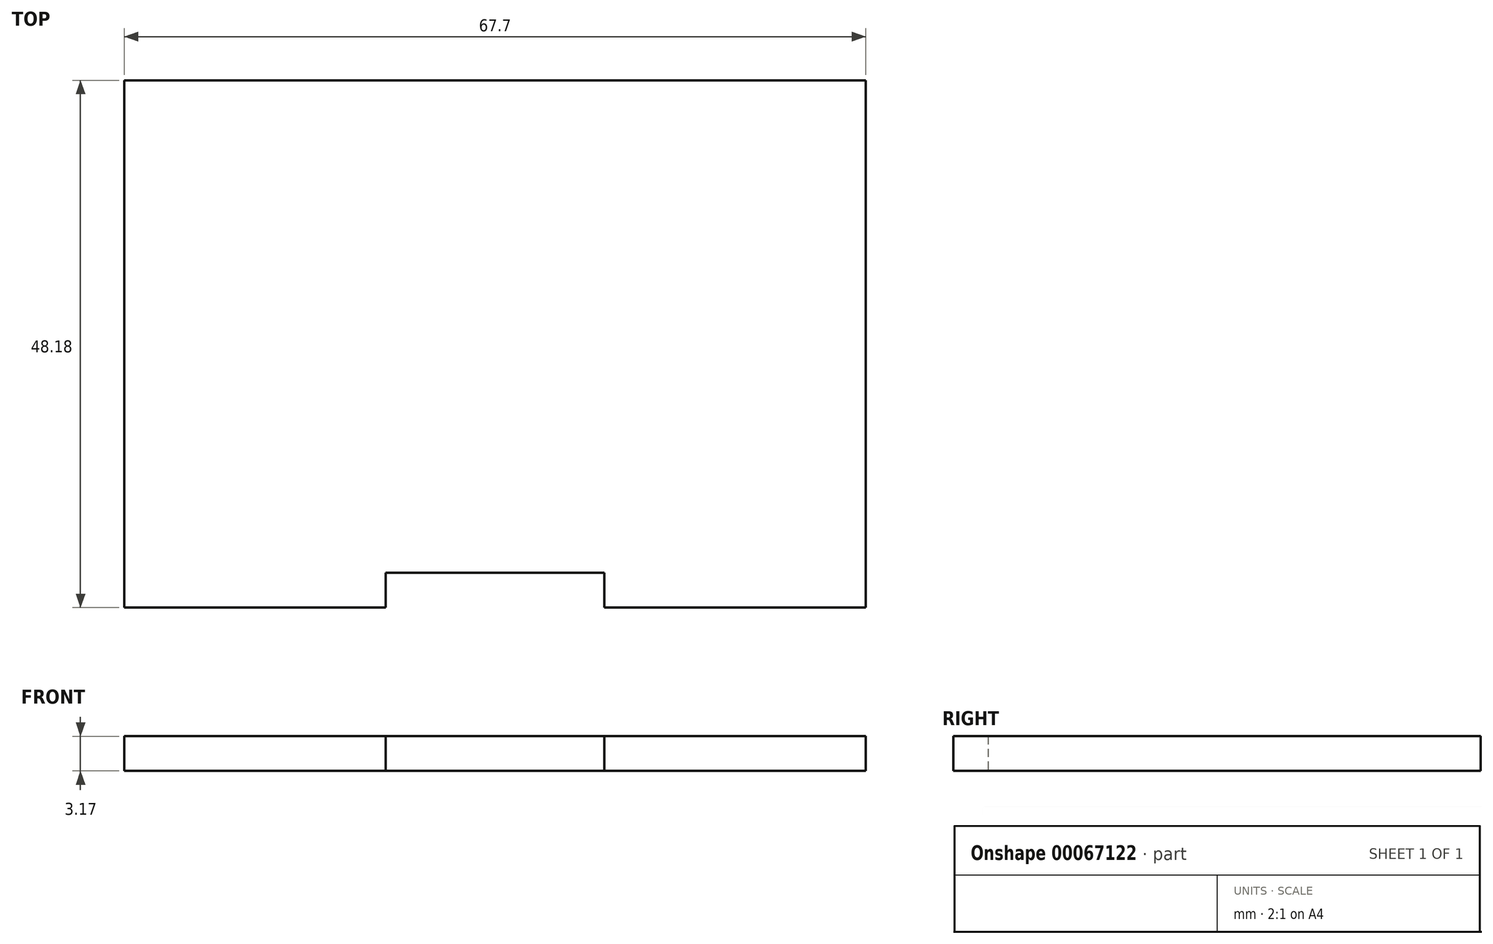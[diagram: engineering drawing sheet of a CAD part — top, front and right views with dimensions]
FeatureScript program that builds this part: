
annotation { "Feature Type Name" : "Feature", "Feature Type Description" : "" }
export const myFeature = defineFeature(function(context is Context, id is Id, definition is map)
    precondition{}
    {
        {
            var Q0;
            Q0=qCreatedBy(makeId("Top.planeOp"),FACE);
            var sketch = newSketch(context, id + "F0", { "sketchPlane" : qUnion([Q0])});
            skLineSegment(sketch, "E0.bottom", {"start": v(-33.85, 0) * mm, "end": v(33.85, 0) * mm});
            skLineSegment(sketch, "E0.top", {"start": v(-33.85, -48.17) * mm, "end": v(33.85, -48.17) * mm});
            skLineSegment(sketch, "E0.left", {"start": v(-33.85, 0) * mm, "end": v(-33.85, -48.17) * mm});
            skLineSegment(sketch, "E0.right", {"start": v(33.85, 0) * mm, "end": v(33.85, -48.17) * mm});
            skLineSegment(sketch, "E1.bottom", {"start": v(-10, -48.17) * mm, "end": v(10, -48.17) * mm});
            skLineSegment(sketch, "E1.top", {"start": v(-10, -45) * mm, "end": v(10, -45) * mm});
            skLineSegment(sketch, "E1.left", {"start": v(-10, -48.17) * mm, "end": v(-10, -45) * mm});
            skLineSegment(sketch, "E1.right", {"start": v(10, -48.17) * mm, "end": v(10, -45) * mm});
            skLineSegment(sketch, "E2", {"start": v(-10, -45) * mm, "end": v(-33.85, -48.18) * mm, "construction": true});
            skLineSegment(sketch, "E3", {"start": v(10, -45) * mm, "end": v(33.85, -48.18) * mm, "construction": true});
            skSolve(sketch);
        }
        {
            var Q0;
            Q0=makeQuery(id+"F0.imprint","IMPRINT",FACE,{"disambiguationData":[TD([[makeQuery(id+"F0.imprint","IMPRINT",EDGE,{"derivedFrom":sQuery(id+"F0.wireOp",EDGE,"E0.bottom")}),-1.0]])]});
            extrude(context, id + "F1", {"entities" : qUnion([Q0]), "depth" : 3.17 * mm});
        }
    });
